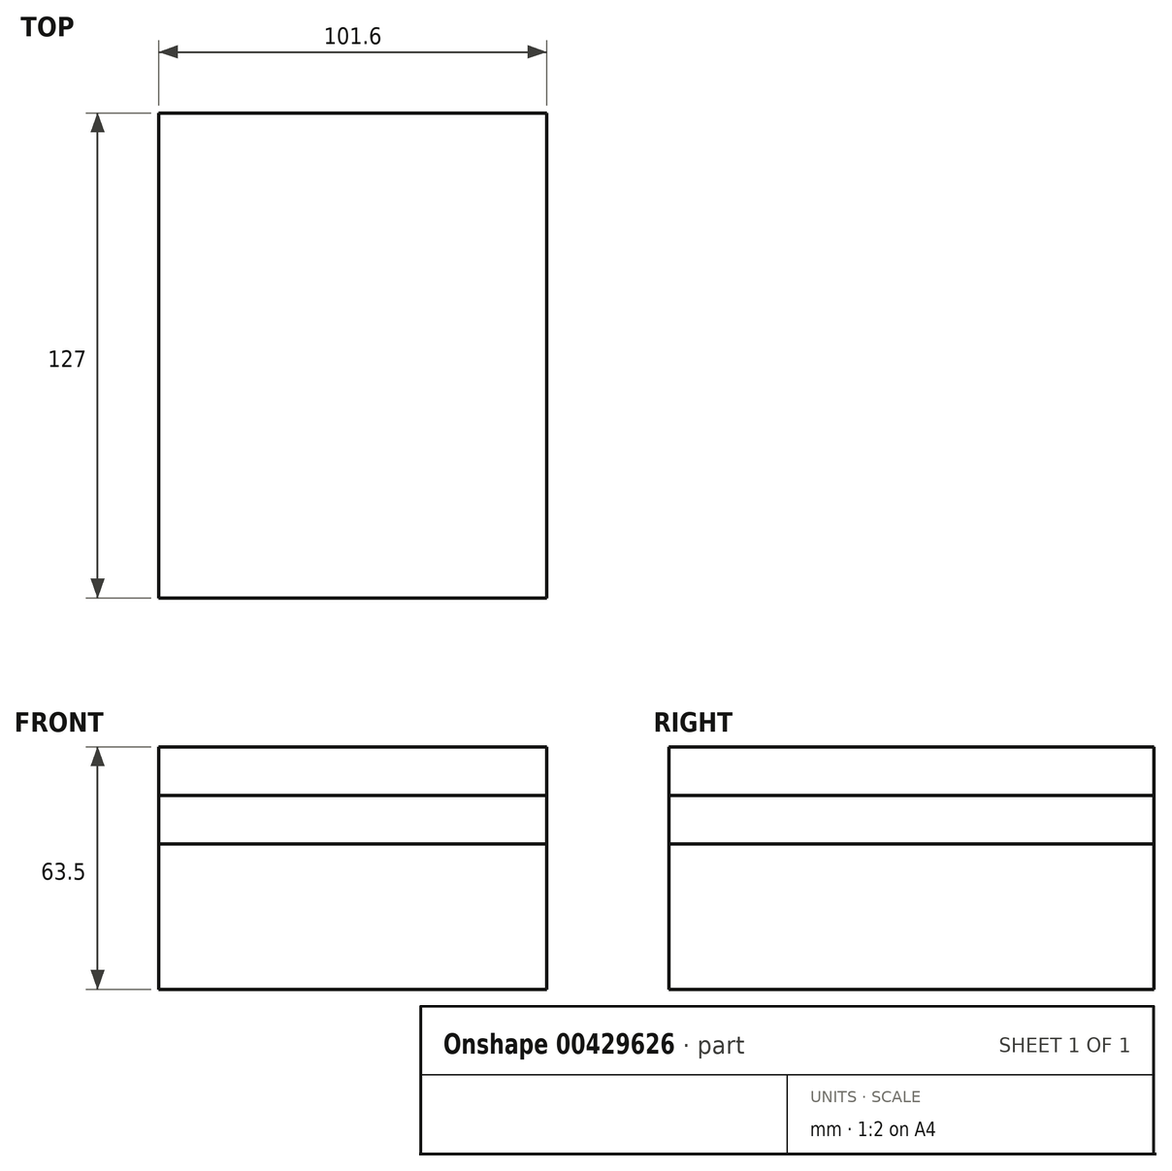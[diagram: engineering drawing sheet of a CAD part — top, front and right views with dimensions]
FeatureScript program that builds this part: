
annotation { "Feature Type Name" : "Feature", "Feature Type Description" : "" }
export const myFeature = defineFeature(function(context is Context, id is Id, definition is map)
    precondition{}
    {
        {
            var Q0;
            Q0=qCreatedBy(makeId("Front.planeOp"),FACE);
            var sketch = newSketch(context, id + "F0", { "sketchPlane" : qUnion([Q0])});
            skLineSegment(sketch, "E0.bottom", {"start": v(53.32, 25.4) * mm, "end": v(-48.28, 25.4) * mm});
            skLineSegment(sketch, "E0.top", {"start": v(53.32, -25.4) * mm, "end": v(-48.28, -25.4) * mm});
            skLineSegment(sketch, "E0.left", {"start": v(53.32, 25.4) * mm, "end": v(53.32, -25.4) * mm});
            skLineSegment(sketch, "E0.right", {"start": v(-48.28, 25.4) * mm, "end": v(-48.28, -25.4) * mm});
            skPoint(sketch, "E0.middle", {"position": v(2.52, 0) * mm});
            skLineSegment(sketch, "E1.bottom", {"start": v(167.62, 88.9) * mm, "end": v(91.42, 88.9) * mm});
            skLineSegment(sketch, "E1.top", {"start": v(167.62, 38.1) * mm, "end": v(91.42, 38.1) * mm});
            skLineSegment(sketch, "E1.left", {"start": v(167.62, 88.9) * mm, "end": v(167.62, 38.1) * mm});
            skLineSegment(sketch, "E1.right", {"start": v(91.42, 88.9) * mm, "end": v(91.42, 38.1) * mm});
            skPoint(sketch, "E1.middle", {"position": v(129.52, 63.5) * mm});
            skLineSegment(sketch, "E2", {"start": v(53.32, 25.4) * mm, "end": v(53.32, 38.1) * mm});
            skArc(sketch, "E3", {"start": v(53.32, 38.1) * mm, "mid": v(64.48, 65.04) * mm, "end": v(91.42, 76.2) * mm});
            skLineSegment(sketch, "E4", {"start": v(91.42, 76.2) * mm, "end": v(104.12, 76.2) * mm});
            skLineSegment(sketch, "E5.0", {"start": v(40.62, 25.4) * mm, "end": v(40.62, 38.1) * mm});
            skArc(sketch, "E6.0", {"start": v(40.62, 38.1) * mm, "mid": v(55.5, 74.02) * mm, "end": v(91.42, 88.9) * mm});
            skFitSpline(sketch, "E7", {"points": [v(-48.28, 25.4) * mm, v(91.42, 88.9) * mm], "startDerivative": vector(287.69, 56.97) * mm, "endDerivative": vector(301.03, 10.77) * mm});
            skSolve(sketch);
        }
        {
            var Q0;
            Q0=makeQuery(id+"F0.imprint","IMPRINT",FACE,{"disambiguationData":[TD([[makeQuery(id+"F0.imprint","IMPRINT",EDGE,{"derivedFrom":sQuery(id+"F0.wireOp",EDGE,"E0.top")}),-1.0]])]});
            extrude(context, id + "F1", {"entities" : qUnion([Q0]), "endBound" : BoundingType.SYMMETRIC, "depth" : 127 * mm});
        }
        {
            var Q0;
            Q0=makeQuery(id+"F1.opExtrude","SWEPT_FACE",FACE,{"disambiguationData":[OSD([sQuery(id+"F0.wireOp",EDGE,"E0.bottom")])]});
            extrude(context, id + "F2", {"entities" : qUnion([Q0]), "endBound" : BoundingType.SYMMETRIC, "depth" : 25.4 * mm});
        }
    });
